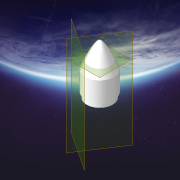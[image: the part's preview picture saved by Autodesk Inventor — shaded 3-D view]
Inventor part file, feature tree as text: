
AUTODESK INVENTOR PART (.ipt)
format: ipt  version: 2020.1 (Build 241239000, 239)  size: 596,480 bytes
history: native  units: mm
features: sketch x9, fillet x8, extrude x7, plane x5, delete_face x3, loft x2, other x2, shell x1, split x1
ambient origin geometry x8: Origin, YZ Plane, XZ Plane, XY Plane, X Axis, Y Axis, Z Axis, Center Point
bodies: Solid1 (feature_tree), Solid2 (feature_tree), Solid3 (feature_tree)
feature tree (38):
  extrude  "Extrusion1"  Depth=70.0mm TaperAngle=0.0deg
  plane  "Work Plane1"
  loft  "Loft1"
  fillet  "Fillet1"  Radius=25.0mm
  plane  "Work Plane2"
  loft  "Loft2"
  shell  "Shell1"  Thickness=0.0mm
  extrude  "Extrusion2"  Depth=2.5mm
  fillet  "Fillet2"  Radius=33.0mm
  extrude  "Extrusion3"  Depth=25.0mm
  extrude  "Extrusion4"  Depth=5.0mm
  fillet  "Fillet3"  Radius=10.0mm
  fillet  "Fillet4"  Radius=10.0mm
  fillet  "Fillet5"  Radius=10.0mm
  fillet  "Fillet6"  Radius=5.0mm
  fillet  "Fillet7"  Radius=25.0mm
  split  "Split1"
  delete_face  "Delete Face1"
  delete_face  "Delete Face2"
  extrude  "Extrusion5"  Depth=5.0mm
  fillet  "Fillet8"  Radius=2.5mm
  plane  "Work Plane3"
  extrude  "Extrusion6"  Depth=10.0mm
  extrude  "Extrusion7"  Depth=10.0mm
  delete_face  "Delete Face8"
  plane  "Work Plane4"
  plane  "Work Plane5"
  sketch  "Sketch1"  dims[d0=55.0mm d1=70.0mm d2=0.0mm]
  sketch  "Sketch4"  dims[d4=45.0mm d5=0.0mm d6=90.0deg d7=5.0mm d8=90.0deg d9=25.0mm]
  other  "Edges1"
  sketch  "Sketch5"  dims[d10=20.0mm d11=30.0mm d12=0.0mm d13=90.0deg]
  other  "Edges2"
  sketch  "Sketch6"  dims[d14=0.0mm d15=90.0deg d16=2.5mm d17=33.0mm]
  sketch  "Sketch7"  dims[d18=15.0mm d19=0.0mm d20=25.0mm]
  sketch  "Sketch8"  dims[d21=5.0mm d22=5.0mm d23=10.0mm d24=10.0mm d25=10.0mm d26=0.0mm d27=5.0mm d28=25.0mm d29=0.0mm]
  sketch  "Sketch9"  dims[d30=5.0mm d31=5.0mm d32=2.5mm]
  sketch  "Sketch12"  dims[d33=5.0mm d34=10.0mm]
  sketch  "Sketch13"  dims[d35=10.0mm d36=10.0mm d37=2.0mm d38=20.0mm d39=0.0mm d40=25.0mm d41=-60.0mm d42=26.0mm d43=26.0mm d44=45.0mm d45=45.0mm d46=7.0mm d47=0.0mm d48=27.0mm d49=27.0mm d50=2.0mm d51=0.0mm]
